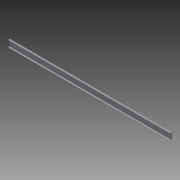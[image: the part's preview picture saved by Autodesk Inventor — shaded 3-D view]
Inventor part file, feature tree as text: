
AUTODESK INVENTOR PART (.ipt)
format: ipt  version: 2013 (Build 170138000, 138)  size: 78,848 bytes
history: native  units: in
note: dims shown in document units (in); Inventor stores cm internally (conversion verified against a paired STEP export)
features: other x2, extrude x1, sketch x1
ambient origin geometry x8: Origin, YZ Plane, XZ Plane, XY Plane, X Axis, Y Axis, Z Axis, Center Point
bodies: Solid1 (feature_tree)
feature tree (4):
  other  "Table"
  other  "Part1-01"
  extrude  "Extrusion1"  Depth=1.0in
  sketch  "Sketch1"  dims[d0=4.0in d1=1.0in d2=0.125in d4=0.0in]
